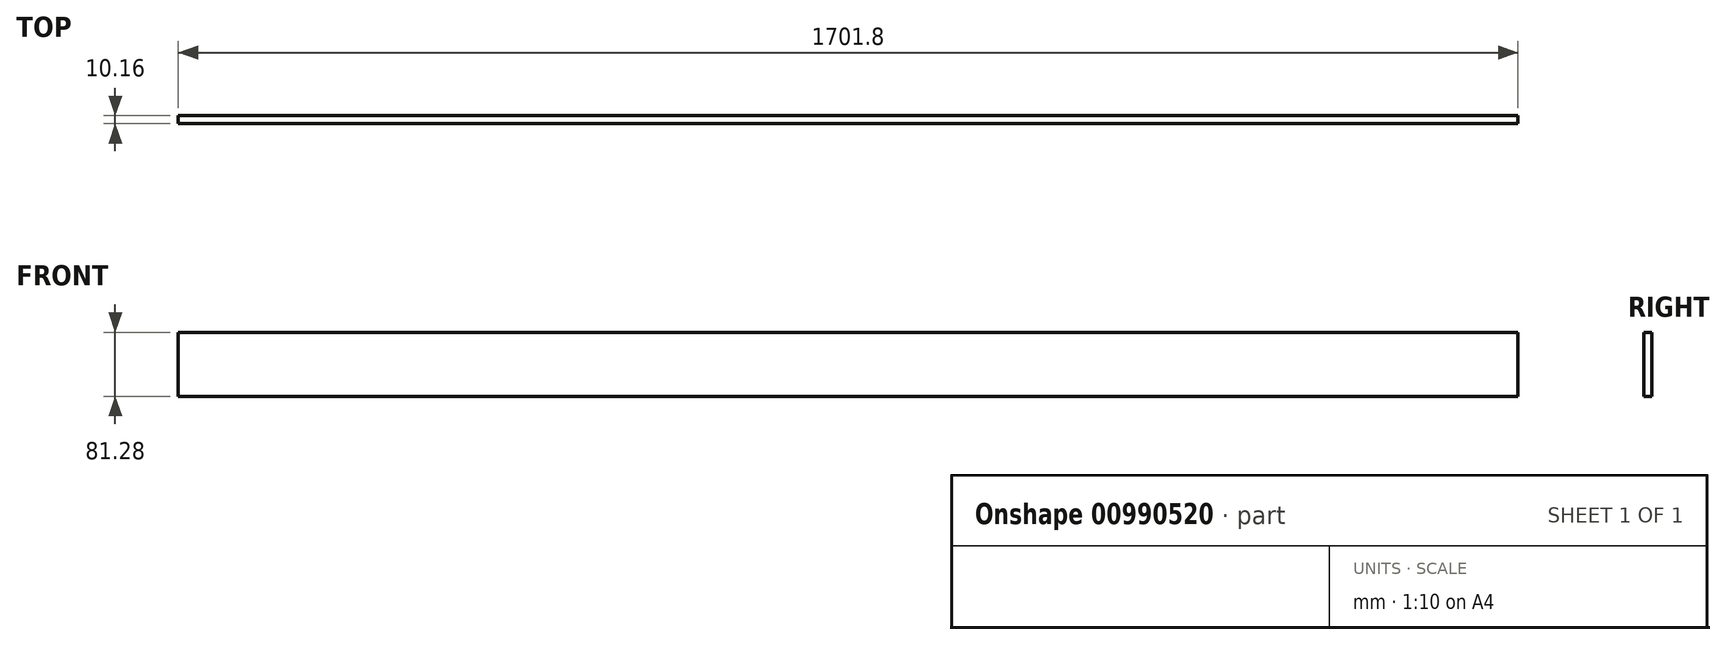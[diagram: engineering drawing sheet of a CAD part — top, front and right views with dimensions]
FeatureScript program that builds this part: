
annotation { "Feature Type Name" : "Feature", "Feature Type Description" : "" }
export const myFeature = defineFeature(function(context is Context, id is Id, definition is map)
    precondition{}
    {
        {
            var Q0;
            Q0=qCreatedBy(makeId("Front.planeOp"),FACE);
            var sketch = newSketch(context, id + "F0", { "sketchPlane" : qUnion([Q0])});
            skLineSegment(sketch, "E0.bottom", {"start": v(-395.3, 81.28) * mm, "end": v(1306.5, 81.28) * mm});
            skLineSegment(sketch, "E0.top", {"start": v(-395.3, 0) * mm, "end": v(1306.5, 0) * mm});
            skLineSegment(sketch, "E0.left", {"start": v(-395.3, 81.28) * mm, "end": v(-395.3, 0) * mm});
            skLineSegment(sketch, "E0.right", {"start": v(1306.5, 81.28) * mm, "end": v(1306.5, 0) * mm});
            skSolve(sketch);
        }
        {
            var Q0;
            Q0 = qSketchRegion(id + "F0", true);
            extrude(context, id + "F1", {"entities" : qUnion([Q0]), "depth" : 10.16 * mm, "offsetDistance" : 25.4 * mm});
        }
    });
